# Revit family: Haworth_BeHold_StorageCabinet
name_source: partatom
category: Furniture Systems
revit_build: Autodesk Revit 2018 (Build: 20170223_1515(x64)
units: mm (PartAtom-declared; Revit-internal decimal feet)

## family parameters
Always vertical = Yes
Cut with Voids When Loaded = No
OmniClass Number = 23.40.70.14.64.21
OmniClass Title = Systems Furniture
Part Type = Normal
Room Calculation Point = No
Round Connector Dimension = Use Diameter
Shared = No
Work Plane-Based = No

## types (4) — shared parameters
Actual Height = 81 "
Actual Shelf 1 = Yes
Actual Shelf 2 = Yes
Actual Shelf 3 = Yes
Actual Shelf 4 = Yes
Assembly Code = E2020200
Base Height = 0.75 "
Classic Pull = No
Cresent Pull = No
Custom Size = No
Description = Haworth - Be_Hold - Freestanding Storage - Storage Cabinet
Door Height = 79.95 "
Height = 81 "
Inset Style = Yes
Linear Pull = Yes
Lock Finish = Haworth _ Paint _ Charcoal
Lock Height = 35 "
Manufacturer = Haworth
Max. Height = 81 "
Max. Width = 36 "
Min. Height = 49 "
Min. Width = 18 "
Model = Haworth Be_Hold
No Pull = No
Panel Thickness = 0.75 "
Proud Style = No
Pull Finish = Haworth _ Paint _ Charcoal
Pull Height = 40 "
Revision Number = 1
Shelf Height 1 = 14.94 "
Shelf Height 2 = 15.25 "
Shelf Height 3 = 15.25 "
Shelf Height 4 = 15.25 "
Size = Verify Final Dim. w/ Haworth
Standard Depths = 16, 24 in
Standard Height = 49-81 in. @ 8 in. increments
Standard Widths = 18-36 in. @ 6 in. increments
Sustainability Info = https://www.haworth.com
URL = www.haworth.com
URL - Product = https://www.haworth.com
Wing Pull = No
With Lock = Yes

## per-type parameters (varying)
| type | 16in. Depth | 24in. Depth | Actual Depth | Actual Width | Double Door Width | Double Doors | Inset Style Width | Shelf Depth | Shelf Width | Single Door | Single Door Width | Width |
| 81h 36w 16d | Yes | No | 16 " | 36 " | 17.88 " | Yes | 15.81 " | 15.25 " | 34.5 " | No | 36 " | 36 " |
| 81h 18w 16d | Yes | No | 16 " | 18 " | 8.88 " | No | 15.81 " | 15.25 " | 16.5 " | Yes | 18 " | 18 " |
| 81h 36w 24d | No | Yes | 24 " | 36 " | 17.88 " | Yes | 23.81 " | 23.25 " | 34.5 " | No | 36 " | 36 " |
| 81h 18w 24d | No | Yes | 24 " | 18 " | 8.88 " | No | 23.81 " | 23.25 " | 16.5 " | Yes | 18 " | 18 " |

## geometry (parser evidence)
native form markers: Sweep x10
no freeform markers — native parametric forms only
